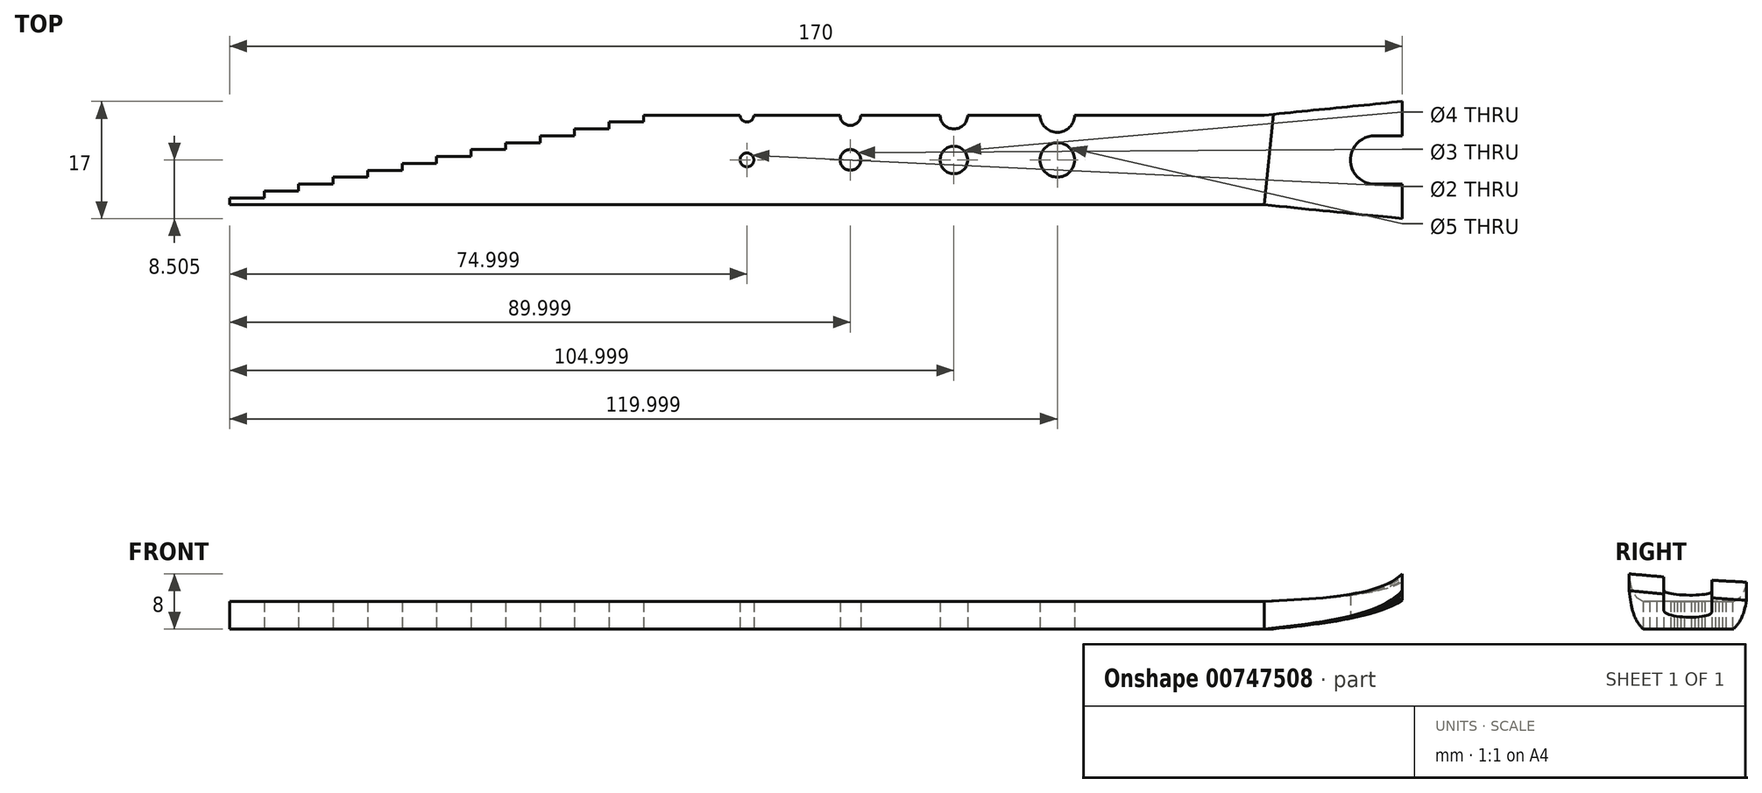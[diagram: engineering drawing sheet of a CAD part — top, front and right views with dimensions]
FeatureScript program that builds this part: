
annotation { "Feature Type Name" : "Feature", "Feature Type Description" : "" }
export const myFeature = defineFeature(function(context is Context, id is Id, definition is map)
    precondition{}
    {
        {
            var Q0;
            Q0=qCreatedBy(makeId("Top.planeOp"),FACE);
            var sketch = newSketch(context, id + "F0", { "sketchPlane" : qUnion([Q0])});
            skLineSegment(sketch, "E0", {"start": v(-52.07, -15.9) * mm, "end": v(-57.07, -15.9) * mm});
            skLineSegment(sketch, "E1", {"start": v(-57.07, -15.9) * mm, "end": v(-57.07, -16.9) * mm});
            skLineSegment(sketch, "E2", {"start": v(-57.07, -16.9) * mm, "end": v(-62.07, -16.9) * mm});
            skLineSegment(sketch, "E3", {"start": v(-62.07, -16.9) * mm, "end": v(-62.07, -17.9) * mm});
            skLineSegment(sketch, "E4", {"start": v(-62.07, -17.9) * mm, "end": v(-67.07, -17.9) * mm});
            skLineSegment(sketch, "E5", {"start": v(-67.07, -17.9) * mm, "end": v(-67.07, -18.9) * mm});
            skLineSegment(sketch, "E6", {"start": v(-67.07, -18.9) * mm, "end": v(-72.07, -18.9) * mm});
            skLineSegment(sketch, "E7", {"start": v(-72.07, -18.9) * mm, "end": v(-72.07, -19.9) * mm});
            skLineSegment(sketch, "E8", {"start": v(-72.07, -19.9) * mm, "end": v(-77.07, -19.9) * mm});
            skLineSegment(sketch, "E9", {"start": v(-77.07, -19.9) * mm, "end": v(-77.07, -20.9) * mm});
            skLineSegment(sketch, "E10", {"start": v(-77.07, -20.9) * mm, "end": v(-82.07, -20.9) * mm});
            skLineSegment(sketch, "E11", {"start": v(-82.07, -20.9) * mm, "end": v(-82.07, -21.9) * mm});
            skLineSegment(sketch, "E12", {"start": v(-82.07, -21.9) * mm, "end": v(-87.07, -21.9) * mm});
            skLineSegment(sketch, "E13", {"start": v(-87.07, -21.9) * mm, "end": v(-87.07, -22.9) * mm});
            skLineSegment(sketch, "E14", {"start": v(-87.07, -22.9) * mm, "end": v(-92.07, -22.9) * mm});
            skLineSegment(sketch, "E15", {"start": v(-92.07, -22.9) * mm, "end": v(-92.07, -23.9) * mm});
            skLineSegment(sketch, "E16", {"start": v(-92.07, -23.9) * mm, "end": v(-97.07, -23.9) * mm});
            skLineSegment(sketch, "E17", {"start": v(-97.07, -23.9) * mm, "end": v(-97.07, -24.9) * mm});
            skLineSegment(sketch, "E18", {"start": v(-102.07, -25.9) * mm, "end": v(-102.07, -24.9) * mm});
            skLineSegment(sketch, "E19", {"start": v(-102.07, -24.9) * mm, "end": v(-97.07, -24.9) * mm});
            skLineSegment(sketch, "E20", {"start": v(-52.07, -15.9) * mm, "end": v(-52.07, -14.9) * mm});
            skLineSegment(sketch, "E21", {"start": v(-52.07, -14.9) * mm, "end": v(-47.07, -14.9) * mm});
            skLineSegment(sketch, "E22", {"start": v(-47.07, -14.9) * mm, "end": v(-47.07, -13.9) * mm});
            skLineSegment(sketch, "E23", {"start": v(-47.07, -13.9) * mm, "end": v(-42.07, -13.9) * mm});
            skLineSegment(sketch, "E24", {"start": v(-42.07, -13.9) * mm, "end": v(-42.07, -12.9) * mm});
            skLineSegment(sketch, "E25", {"start": v(-102.07, -25.9) * mm, "end": v(47.93, -25.9) * mm});
            skLineSegment(sketch, "E26", {"start": v(47.93, -25.9) * mm, "end": v(47.93, -12.9) * mm});
            skLineSegment(sketch, "E27", {"start": v(47.93, -12.9) * mm, "end": v(20.43, -12.9) * mm});
            skPoint(sketch, "E28.endSnap0", {"position": v(-54.57, -15.9) * mm});
            skCircle(sketch, "E29", {"center": v(-27.07, -19.4) * mm, "radius": 1 * mm});
            skCircle(sketch, "E30", {"center": v(-12.07, -19.4) * mm, "radius": 1.5 * mm});
            skCircle(sketch, "E31", {"center": v(2.93, -19.4) * mm, "radius": 2 * mm});
            skCircle(sketch, "E32", {"center": v(17.93, -19.4) * mm, "radius": 2.5 * mm});
            skArc(sketch, "E33", {"start": v(-28.07, -12.9) * mm, "mid": v(-27.07, -13.9) * mm, "end": v(-26.07, -12.9) * mm});
            skArc(sketch, "E34", {"start": v(-13.57, -12.9) * mm, "mid": v(-12.07, -14.4) * mm, "end": v(-10.57, -12.9) * mm});
            skArc(sketch, "E35", {"start": v(0.93, -12.9) * mm, "mid": v(2.93, -14.9) * mm, "end": v(4.93, -12.9) * mm});
            skArc(sketch, "E36", {"start": v(15.43, -12.9) * mm, "mid": v(17.93, -15.4) * mm, "end": v(20.43, -12.9) * mm});
            skLineSegment(sketch, "E37.trimOffspring", {"start": v(-28.07, -12.9) * mm, "end": v(-42.07, -12.9) * mm});
            skLineSegment(sketch, "E38.trimOffspring", {"start": v(-13.57, -12.9) * mm, "end": v(-26.07, -12.9) * mm});
            skLineSegment(sketch, "E39.trimOffspring", {"start": v(0.93, -12.9) * mm, "end": v(-10.57, -12.9) * mm});
            skLineSegment(sketch, "E40.trimOffspring", {"start": v(15.43, -12.9) * mm, "end": v(4.93, -12.9) * mm});
            skSolve(sketch);
        }
        {
            var Q0;
            Q0=makeQuery(id+"F0.imprint","IMPRINT",FACE,{"disambiguationData":[TD([[makeQuery(id+"F0.imprint","IMPRINT",EDGE,{"derivedFrom":sQuery(id+"F0.wireOp",EDGE,"E0")}),1.0]])]});
            extrude(context, id + "F1", {"entities" : qUnion([Q0]), "depth" : 4 * mm, "offsetDistance" : 25 * mm});
        }
        {
            var Q0;
            Q0=makeQuery(id+"F1.opExtrude","CAP_FACE",FACE,{"disambiguationData":[OSD([sQuery(id+"F0.wireOp",EDGE,"E0"),sQuery(id+"F0.wireOp",EDGE,"E1"),sQuery(id+"F0.wireOp",EDGE,"E2"),sQuery(id+"F0.wireOp",EDGE,"E3"),sQuery(id+"F0.wireOp",EDGE,"E4"),sQuery(id+"F0.wireOp",EDGE,"E5"),sQuery(id+"F0.wireOp",EDGE,"E6"),sQuery(id+"F0.wireOp",EDGE,"E7"),sQuery(id+"F0.wireOp",EDGE,"E8"),sQuery(id+"F0.wireOp",EDGE,"E9"),sQuery(id+"F0.wireOp",EDGE,"E10"),sQuery(id+"F0.wireOp",EDGE,"E11"),sQuery(id+"F0.wireOp",EDGE,"E12"),sQuery(id+"F0.wireOp",EDGE,"E13"),sQuery(id+"F0.wireOp",EDGE,"E14"),sQuery(id+"F0.wireOp",EDGE,"E15"),sQuery(id+"F0.wireOp",EDGE,"E16"),sQuery(id+"F0.wireOp",EDGE,"E17"),sQuery(id+"F0.wireOp",EDGE,"E18"),sQuery(id+"F0.wireOp",EDGE,"E19"),sQuery(id+"F0.wireOp",EDGE,"E20"),sQuery(id+"F0.wireOp",EDGE,"E21"),sQuery(id+"F0.wireOp",EDGE,"E22"),sQuery(id+"F0.wireOp",EDGE,"E23"),sQuery(id+"F0.wireOp",EDGE,"E24"),sQuery(id+"F0.wireOp",EDGE,"E25"),sQuery(id+"F0.wireOp",EDGE,"E26"),sQuery(id+"F0.wireOp",EDGE,"E27"),sQuery(id+"F0.wireOp",EDGE,"E29"),sQuery(id+"F0.wireOp",EDGE,"E30"),sQuery(id+"F0.wireOp",EDGE,"E31"),sQuery(id+"F0.wireOp",EDGE,"E32"),sQuery(id+"F0.wireOp",EDGE,"E33"),sQuery(id+"F0.wireOp",EDGE,"E34"),sQuery(id+"F0.wireOp",EDGE,"E35"),sQuery(id+"F0.wireOp",EDGE,"E36"),sQuery(id+"F0.wireOp",EDGE,"E37.trimOffspring"),sQuery(id+"F0.wireOp",EDGE,"E38.trimOffspring"),sQuery(id+"F0.wireOp",EDGE,"E39.trimOffspring"),sQuery(id+"F0.wireOp",EDGE,"E40.trimOffspring")])],"isStart":true});
            var sketch = newSketch(context, id + "F2", { "sketchPlane" : qUnion([Q0])});
            skLineSegment(sketch, "E41", {"start": v(47.93, 12.9) * mm, "end": v(47.93, 25.9) * mm});
            skLineSegment(sketch, "E42", {"start": v(47.93, 25.9) * mm, "end": v(67.93, 27.9) * mm});
            skLineSegment(sketch, "E43", {"start": v(47.93, 12.9) * mm, "end": v(67.93, 10.9) * mm});
            skLineSegment(sketch, "E44", {"start": v(67.93, 27.9) * mm, "end": v(67.93, 22.9) * mm});
            skLineSegment(sketch, "E45", {"start": v(67.93, 10.9) * mm, "end": v(67.93, 15.9) * mm});
            skLineSegment(sketch, "E46", {"start": v(67.93, 15.9) * mm, "end": v(63.93, 15.9) * mm});
            skLineSegment(sketch, "E47", {"start": v(67.93, 22.9) * mm, "end": v(63.93, 22.9) * mm});
            skArc(sketch, "E48", {"start": v(63.93, 15.9) * mm, "mid": v(60.43, 19.4) * mm, "end": v(63.93, 22.9) * mm});
            skSolve(sketch);
        }
        {
            var Q0;
            Q0=makeQuery(id+"F2.imprint","IMPRINT",FACE,{"disambiguationData":[TD([[makeQuery(id+"F2.imprint","IMPRINT",EDGE,{"derivedFrom":sQuery(id+"F2.wireOp",EDGE,"E41")}),1.0]])]});
            extrude(context, id + "F3", {"entities" : qUnion([Q0]), "operationType" : NewBodyOperationType.ADD, "oppositeDirection" : true, "depth" : 8 * mm, "offsetDistance" : 25 * mm});
        }
        {
            var Q0;
            Q0=makeQuery(id+"F3.opExtrude","SWEPT_FACE",FACE,{"disambiguationData":[OSD([sQuery(id+"F2.wireOp",EDGE,"E42")])]});
            var sketch = newSketch(context, id + "F4", { "sketchPlane" : qUnion([Q0])});
            skFitSpline(sketch, "E49", {"points": [v(50.27, 4) * mm, v(70.37, 8) * mm, v(72.3, 17.02) * mm], "startDerivative": vector(42.2, 1.96) * mm, "endDerivative": vector(-0.97, 25.63) * mm});
            skFitSpline(sketch, "E50", {"points": [v(50.27, 0) * mm, v(70.37, 5.57) * mm, v(72.3, 17.02) * mm], "startDerivative": vector(43.85, 4.84) * mm, "endDerivative": vector(-2.02, 30.43) * mm});
            skLineSegment(sketch, "E51", {"start": v(50.27, 19.53) * mm, "end": v(74.87, 19.53) * mm});
            skLineSegment(sketch, "E52", {"start": v(74.87, 19.53) * mm, "end": v(74.87, -3.93) * mm});
            skLineSegment(sketch, "E53", {"start": v(74.87, -3.93) * mm, "end": v(50.27, -3.93) * mm});
            skLineSegment(sketch, "E54", {"start": v(50.27, -3.93) * mm, "end": v(50.27, 0) * mm});
            skLineSegment(sketch, "E55", {"start": v(50.27, 4) * mm, "end": v(47.71, 4) * mm});
            skLineSegment(sketch, "E56", {"start": v(47.71, 4) * mm, "end": v(47.71, 19.53) * mm});
            skLineSegment(sketch, "E57", {"start": v(47.71, 19.53) * mm, "end": v(50.27, 19.53) * mm});
            skSolve(sketch);
        }
        {
            var Q0;
            Q0=makeQuery(id+"F4.imprint","IMPRINT",FACE,{"disambiguationData":[TD([[makeQuery(id+"F4.imprint","IMPRINT",EDGE,{"derivedFrom":sQuery(id+"F4.wireOp",EDGE,"E51")}),-1.0]])]});
            var Q1;
            {var subQ1=sQuery(id+"F2.wireOp",EDGE,"E42");var subQ2=makeQuery(id+"F3.opExtrude","CAP_EDGE",EDGE,{"disambiguationData":[OSD([subQ1])],"isStart":false});Q1=makeQuery(id+"F4.imprint","IMPRINT",FACE,{"disambiguationData":[TD([[makeQuery(id+"F4.imprint","IMPRINT",EDGE,{"derivedFrom":subQ2}),-1.0]])]});}
            var Q2;
            {var subQ1=sQuery(id+"F2.wireOp",EDGE,"E42");var subQ3=makeQuery(id+"F3.opExtrude","CAP_EDGE",EDGE,{"disambiguationData":[OSD([subQ1])],"isStart":true});Q2=makeQuery(id+"F4.imprint","IMPRINT",FACE,{"disambiguationData":[TD([[makeQuery(id+"F4.imprint","IMPRINT",EDGE,{"derivedFrom":subQ3}),1.0]])]});}
            extrude(context, id + "F5", {"entities" : qUnion([Q0, Q1, Q2]), "operationType" : NewBodyOperationType.REMOVE, "oppositeDirection" : true, "depth" : 25 * mm, "offsetDistance" : 25 * mm});
        }
    });
